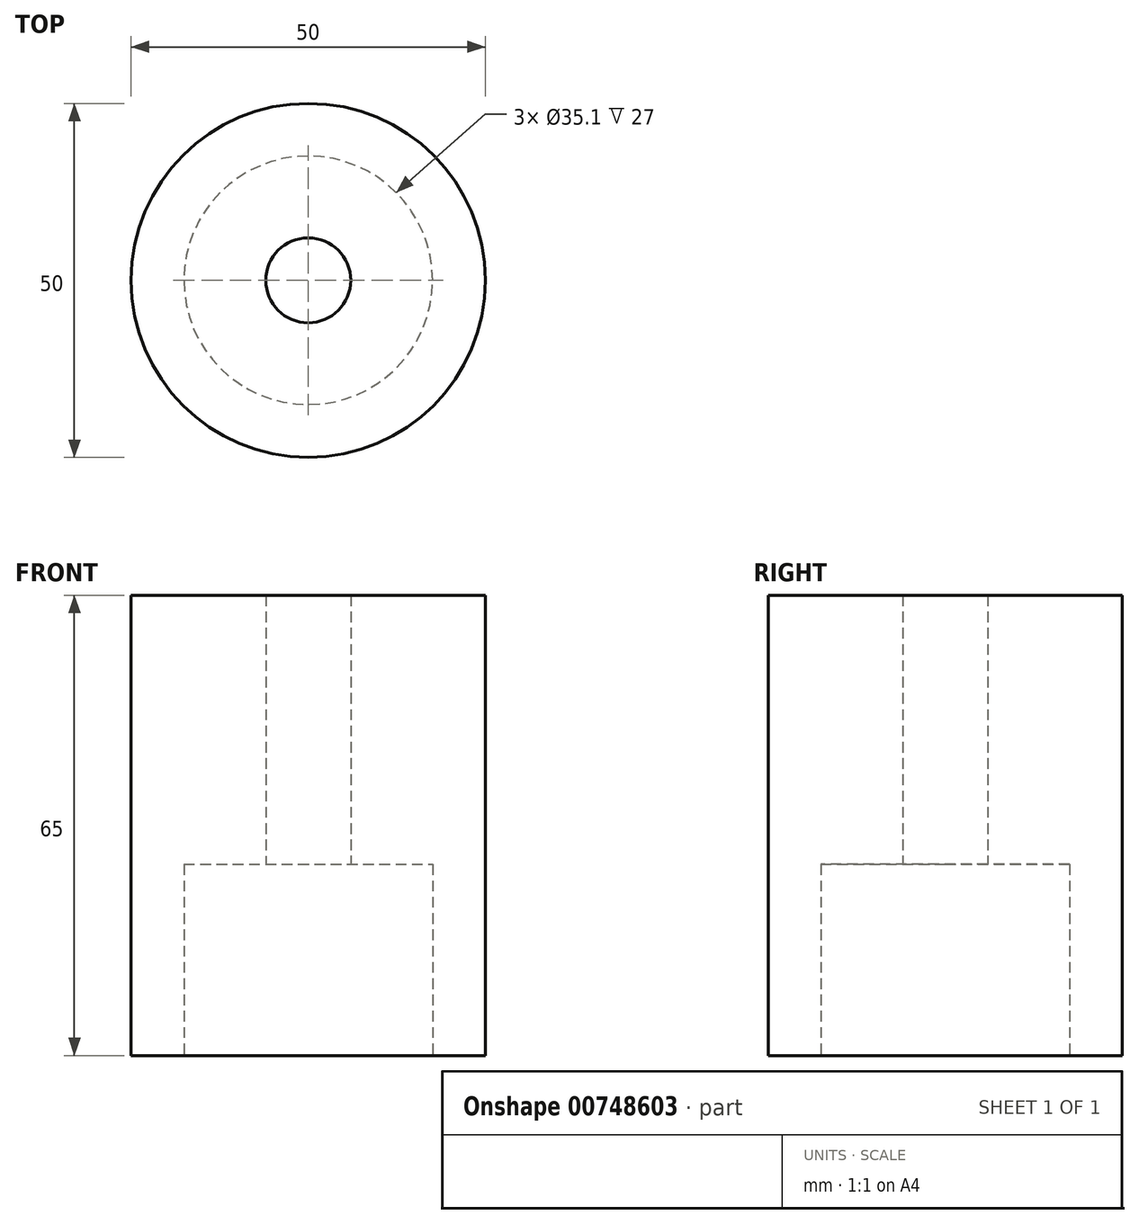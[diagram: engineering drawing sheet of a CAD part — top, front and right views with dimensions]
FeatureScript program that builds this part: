
annotation { "Feature Type Name" : "Feature", "Feature Type Description" : "" }
export const myFeature = defineFeature(function(context is Context, id is Id, definition is map)
    precondition{}
    {
        {
            var Q0;
            Q0=qCreatedBy(makeId("Top.planeOp"),FACE);
            var sketch = newSketch(context, id + "F0", { "sketchPlane" : qUnion([Q0])});
            skCircle(sketch, "E0", {"center": v(0, 0) * mm, "radius": 25 * mm});
            skCircle(sketch, "E1", {"center": v(0, 0) * mm, "radius": 17.55 * mm});
            skSolve(sketch);
        }
        {
            var Q0;
            Q0=makeQuery(id+"F0.imprint","IMPRINT",FACE,{"disambiguationData":[TD([[makeQuery(id+"F0.imprint","IMPRINT",EDGE,{"derivedFrom":sQuery(id+"F0.wireOp",EDGE,"E0")}),1.0]])]});
            var Q1;
            Q1=makeQuery(id+"F0.imprint","IMPRINT",FACE,{"disambiguationData":[TD([[makeQuery(id+"F0.imprint","IMPRINT",EDGE,{"derivedFrom":sQuery(id+"F0.wireOp",EDGE,"E1")}),1.0]])]});
            extrude(context, id + "F1", {"entities" : qUnion([Q0, Q1]), "depth" : 65 * mm, "offsetDistance" : 25 * mm});
        }
        {
            var Q0;
            Q0=makeQuery(id+"F1.opExtrude","CAP_FACE",FACE,{"disambiguationData":[OSD([sQuery(id+"F0.wireOp",EDGE,"E0")])],"isStart":true});
            var sketch = newSketch(context, id + "F2", { "sketchPlane" : qUnion([Q0])});
            skCircle(sketch, "E2", {"center": v(0, 0) * mm, "radius": 6 * mm});
            skSolve(sketch);
        }
        {
            var Q0;
            Q0 = qSketchRegion(id + "F2", true);
            extrude(context, id + "F3", {"entities" : qUnion([Q0]), "operationType" : NewBodyOperationType.REMOVE, "endBound" : BoundingType.THROUGH_ALL, "oppositeDirection" : true, "depth" : 25 * mm, "offsetDistance" : 25 * mm});
        }
        {
            var Q0;
            Q0=makeQuery(id+"F1.opExtrude","CAP_FACE",FACE,{"disambiguationData":[OSD([sQuery(id+"F0.wireOp",EDGE,"E0")])],"isStart":true});
            var sketch = newSketch(context, id + "F4", { "sketchPlane" : qUnion([Q0])});
            skCircle(sketch, "E3", {"center": v(0, 0) * mm, "radius": 17.55 * mm});
            skSolve(sketch);
        }
        {
            var Q0;
            Q0 = qSketchRegion(id + "F4", true);
            extrude(context, id + "F5", {"entities" : qUnion([Q0]), "operationType" : NewBodyOperationType.REMOVE, "oppositeDirection" : true, "depth" : 27 * mm, "offsetDistance" : 25 * mm});
        }
    });
